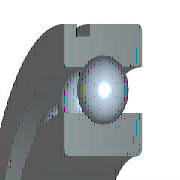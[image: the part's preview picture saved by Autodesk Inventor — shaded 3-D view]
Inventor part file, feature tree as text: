
AUTODESK INVENTOR PART (.ipt)
format: ipt  version: 2015 (Build 190159000, 159)  size: 320,000 bytes
history: native  units: mm (DEFAULTED — no unit token found)
features: sketch x1, other x1, pattern_circular x1
ambient origin geometry x8: Origin, YZ Plane, XZ Plane, XY Plane, X Axis, Y Axis, Z Axis, Center Point
bodies: Solid1 (feature_tree)
feature tree (3):
  sketch  "草图"  dims[d0=10.4mm d17=90.0deg d18=90.0deg d1=1.1mm d2=90.0mm d3=360.0deg d4=0.0mm d5=0.0mm d6=0.0mm d7=40.0mm d8=80.0mm d9=60.0mm d10=76.04mm d11=53.04mm d12=53.04mm d13=53.04mm d14=0.0mm d15=18.0mm d16=18.0mm d19=3.0mm d20=6.0mm d22=9.0mm d23=0.0mm d24=0.0mm]
  other  "轴承体"
  pattern_circular  "IDS_ARRAYBALL[SIMPL:T]"  Angle=90.0deg  [1 undecoded]
note: 1 required parameter value undecoded (feature->parameter linkage not recoverable at this tier; creation-order binding heuristic only, values carry confidence <= 0.55)
